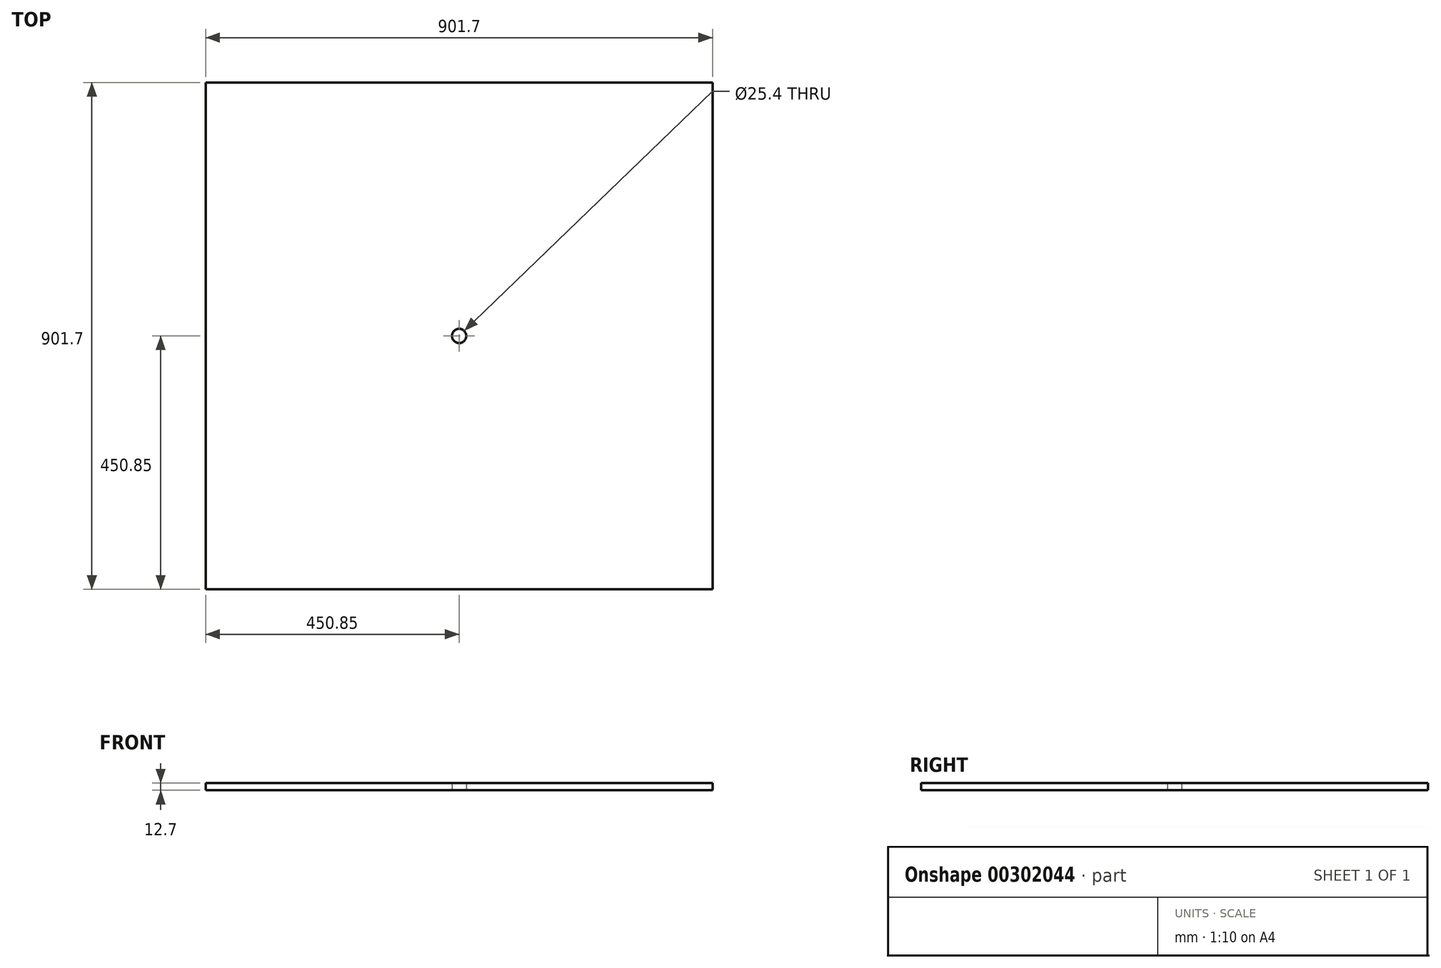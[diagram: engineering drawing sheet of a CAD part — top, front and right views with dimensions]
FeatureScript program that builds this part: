
annotation { "Feature Type Name" : "Feature", "Feature Type Description" : "" }
export const myFeature = defineFeature(function(context is Context, id is Id, definition is map)
    precondition{}
    {
        {
            var Q0;
            Q0=qCreatedBy(makeId("Top.planeOp"),FACE);
            var sketch = newSketch(context, id + "F0", { "sketchPlane" : qUnion([Q0])});
            skLineSegment(sketch, "E0.bottom", {"start": v(-450.85, 450.85) * mm, "end": v(450.85, 450.85) * mm});
            skLineSegment(sketch, "E0.top", {"start": v(-450.85, -450.85) * mm, "end": v(450.85, -450.85) * mm});
            skLineSegment(sketch, "E0.left", {"start": v(-450.85, 450.85) * mm, "end": v(-450.85, -450.85) * mm});
            skLineSegment(sketch, "E0.right", {"start": v(450.85, 450.85) * mm, "end": v(450.85, -450.85) * mm});
            skPoint(sketch, "E0.middle", {"position": v(0, 0) * mm});
            skCircle(sketch, "E1", {"center": v(0, 0) * mm, "radius": 12.7 * mm});
            skSolve(sketch);
        }
        {
            var Q0;
            Q0 = qSketchRegion(id + "F0", true);
            extrude(context, id + "F1", {"entities" : qUnion([Q0]), "depth" : 12.7 * mm});
        }
    });
